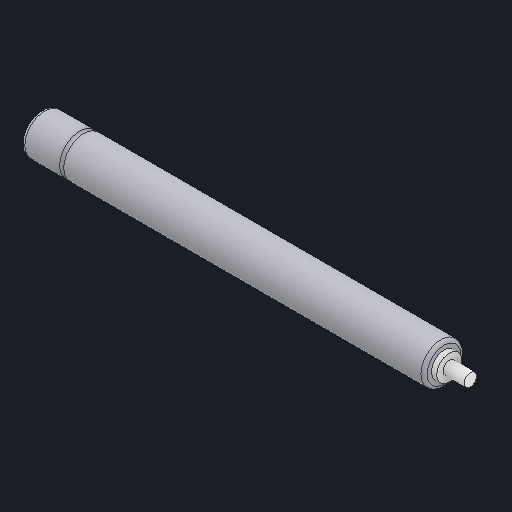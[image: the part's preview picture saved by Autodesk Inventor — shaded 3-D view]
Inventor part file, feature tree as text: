
AUTODESK INVENTOR PART (.ipt)
format: ipt  version: 2023 (Build 270158000, 158)  size: 229,376 bytes
history: native  units: in
note: dims shown in document units (in); Inventor stores cm internally (conversion verified against a paired STEP export)
features: revolve x7
ambient origin geometry x8: Origin, YZ Plane, XZ Plane, XY Plane, X Axis, Y Axis, Z Axis, Center Point
bodies: Solid1 (feature_tree), Solid2 (feature_tree), Solid3 (feature_tree), Solid4 (feature_tree), Solid5 (feature_tree), Solid6 (feature_tree), Solid7 (feature_tree)
feature tree (7):
  revolve  "Revolve1"  [1 undecoded]
  revolve  "Revolve2"  [1 undecoded]
  revolve  "Revolve3"  [1 undecoded]
  revolve  "Revolve4"  [1 undecoded]
  revolve  "Revolve5"  [1 undecoded]
  revolve  "Revolve6"  [1 undecoded]
  revolve  "Revolve7"  [1 undecoded]
note: 7 required parameter values undecoded (feature->parameter linkage not recoverable at this tier; creation-order binding heuristic only, values carry confidence <= 0.55)
